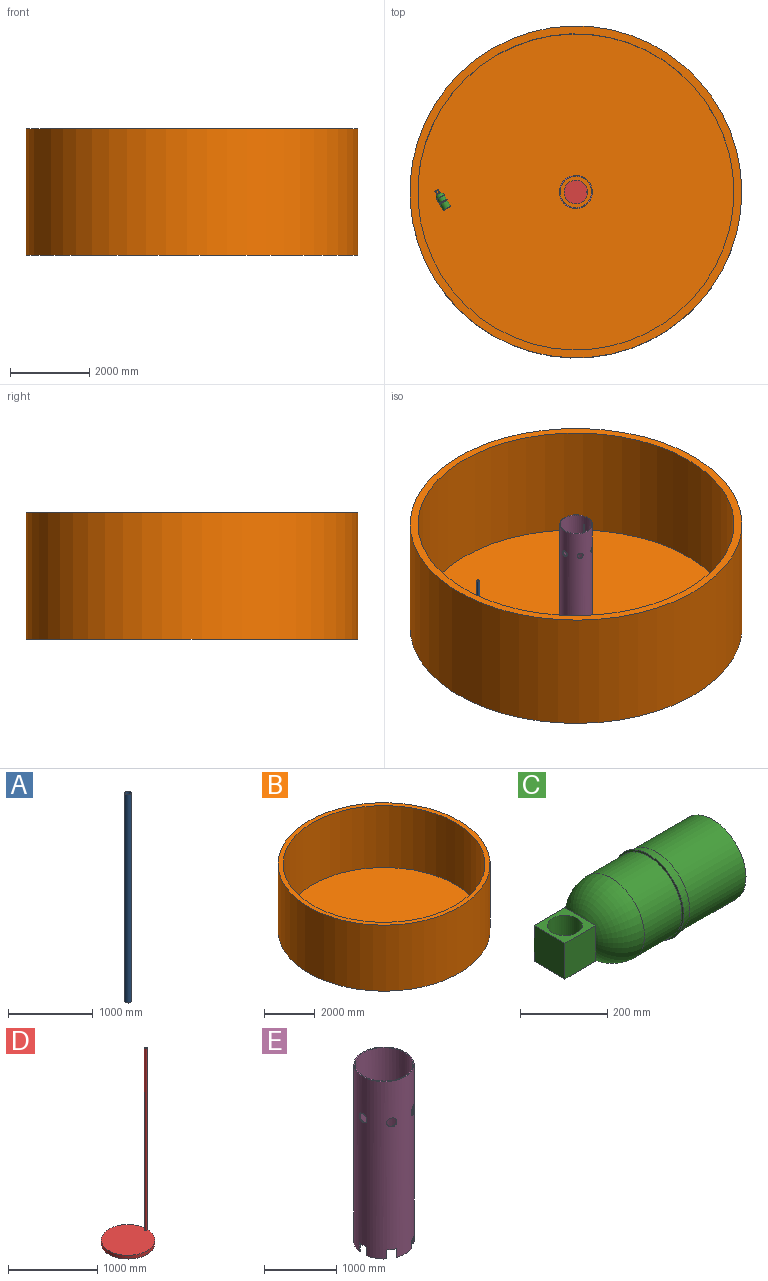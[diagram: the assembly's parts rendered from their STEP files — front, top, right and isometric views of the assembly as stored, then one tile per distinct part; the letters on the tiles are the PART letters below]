
ASSEMBLY  parts=5 mates=4
PART A: 4 faces, bbox 80x80x3000 mm
  f0: cylinder r=39mm len=3000mm, axis (0,0,-1), area 735132.7mm2, adj f2,f3
  f1: cylinder r=40mm len=3000mm, axis (0,0,-1), area 753982.2mm2, adj f2,f3
  f2: plane 80x80mm, normal (0,0,1), area 248.2mm2, adj f0,f1
  f3: plane 80x80mm, normal (0,0,-1), area 248.2mm2, adj f0,f1
PART B: 5 faces, bbox 8400x8400x3200 mm
  f0: cylinder r=4200mm len=8400mm, axis (0,0,1), area 84446010.5mm2, adj f1,f3
  f1: plane 8400x8400mm, normal (0,0,-1), area 55417694.4mm2, adj f0
  f2: cylinder r=4000mm len=8000mm, axis (0,0,-1), area 75398223.7mm2, adj f3,f4
  f3: plane 8400x8400mm, normal (0,0,1), area 5152212mm2, adj f0,f2
  f4: plane 8000x8000mm, normal (0,0,1), area 50265482.5mm2, adj f2
PART C: 13 faces, bbox 528x227x227 mm
  f0: cylinder r=108mm len=216mm, axis (1,0,0), area 82196.7mm2, adj f1,f5
  f1: torus R=8mm, axis (1,0,0), area 70123.6mm2, adj f0,f6
  f2: plane 216x216mm, normal (1,0,0), area 36643.5mm2, adj f3
  f3: cylinder r=108mm len=216mm, axis (1,0,0), area 123631.8mm2, adj f2,f4
  f4: cone r=113.5mm half-angle=12.4deg, axis (-1,0,0), area 17812.6mm2, adj f3,f5
  f5: plane 227x227mm, normal (-1,0,0), area 3827.2mm2, adj f0,f4
  f6: plane 100x100mm, normal (1,0,0), area 9195.8mm2, adj f1,f7,f9,f10,f11
  f7: plane 100x100mm, normal (0,1,0), area 10000mm2, adj f6,f8,f10,f11
  f8: plane 100x100mm, normal (-1,0,0), area 10000mm2, adj f7,f9,f10,f11
  f9: plane 100x100mm, normal (0,-1,0), area 10000mm2, adj f6,f8,f10,f11
  f10: plane 100x100mm, normal (0,0,1), area 4973.5mm2, adj f6,f7,f8,f9,f12
  f11: plane 100x100mm, normal (0,0,-1), area 4973.5mm2, adj f6,f7,f8,f9,f12
  f12: cylinder r=40mm len=100mm, axis (0,0,1), area 25132.7mm2, adj f10,f11
PART D: 7 faces, bbox 600x600x2550 mm
  f0: cylinder r=300mm len=600mm, axis (0,0,-1), area 94247.8mm2, adj f1,f2
  f1: plane 600x600mm, normal (0,0,1), area 281939.1mm2, adj f0,f4
  f2: plane 600x600mm, normal (0,0,-1), area 282743.3mm2, adj f0
  f3: cylinder r=14mm len=2500mm, axis (0,0,-1), area 219911.5mm2, adj f5,f6
  f4: cylinder r=16mm len=2500mm, axis (0,0,-1), area 251327.4mm2, adj f1,f5
  f5: plane 32x32mm, normal (0,0,1), area 188.5mm2, adj f3,f4
  f6: plane 28x28mm, normal (0,0,1), area 615.8mm2, adj f3
PART E: 33 faces, bbox 830x830x3000 mm
  f0: plane 129.95x83.55mm, normal (0,0,-1), area 2133.7mm2, adj f5,f6,f27,f31
  f1: plane 144.13x21.08mm, normal (0,0,-1), area 2133.7mm2, adj f5,f6,f24,f28
  f2: plane 129.95x83.55mm, normal (0,0,-1), area 2133.7mm2, adj f5,f6,f21,f25
  f3: plane 129.95x83.55mm, normal (0,0,-1), area 2133.7mm2, adj f5,f6,f18,f22
  f4: plane 144.13x21.08mm, normal (0,0,-1), area 2133.7mm2, adj f5,f6,f15,f19
  f5: cylinder r=415mm len=3000mm, axis (0,0,-1), area 7585657.5mm2, adj f0,f1,f2,f3,f4,f7,f8,f9
  f6: cylinder r=400mm len=3000mm, axis (0,0,-1), area 7307745.1mm2, adj f0,f1,f2,f3,f4,f7,f8,f9
  f7: plane 830x830mm, normal (0,0,1), area 38406mm2, adj f5,f6
  f8: plane 129.95x83.55mm, normal (0,0,-1), area 2133.7mm2, adj f5,f6,f16,f30
  f9: cylinder r=75mm len=150mm, axis (1,0,0), area 7130.8mm2, adj f5,f6
  f10: cylinder r=75mm len=150mm, axis (0.5,-0.87,0), area 7129.7mm2, adj f5,f6
  f11: cylinder r=75mm len=150mm, axis (-0.5,-0.87,0), area 7129.7mm2, adj f5,f6
  f12: cylinder r=75mm len=150mm, axis (-1,0,0), area 7129.7mm2, adj f5,f6
  f13: cylinder r=75mm len=150mm, axis (-0.5,0.87,0), area 7129.7mm2, adj f5,f6
  f14: cylinder r=75mm len=150mm, axis (0.5,0.87,0), area 7129.7mm2, adj f5,f6
  f15: plane 150x14.77mm, normal (0.17,-0.98,0), area 2250mm2, adj f4,f5,f6,f17
  f16: plane 150x11.49mm, normal (-0.77,0.64,0), area 2250mm2, adj f5,f6,f8,f17
  f17: plane 248.45x151.58mm, normal (0,0,-1), area 4267.3mm2, adj f5,f6,f15,f16
  f18: plane 150x11.49mm, normal (-0.77,-0.64,0), area 2250mm2, adj f3,f5,f6,f20
  f19: plane 150x14.77mm, normal (0.17,0.98,0), area 2250mm2, adj f4,f5,f6,f20
  f20: plane 248.45x151.58mm, normal (0,0,-1), area 4267.3mm2, adj f5,f6,f18,f19
  f21: plane 150x14.1mm, normal (-0.94,0.34,0), area 2250mm2, adj f2,f5,f6,f23
  f22: plane 150x14.1mm, normal (0.94,0.34,0), area 2250mm2, adj f3,f5,f6,f23
  f23: plane 283.88x39.12mm, normal (0,0,-1), area 4267.3mm2, adj f5,f6,f21,f22
  f24: plane 150x14.77mm, normal (-0.17,0.98,0), area 2250mm2, adj f1,f5,f6,f26
  f25: plane 150x11.49mm, normal (0.77,-0.64,0), area 2250mm2, adj f2,f5,f6,f26
  f26: plane 248.45x151.58mm, normal (0,0,-1), area 4267.3mm2, adj f5,f6,f24,f25
  f27: plane 150x11.49mm, normal (0.77,0.64,0), area 2250mm2, adj f0,f5,f6,f29
  f28: plane 150x14.77mm, normal (-0.17,-0.98,0), area 2250mm2, adj f1,f5,f6,f29
  f29: plane 248.45x151.58mm, normal (0,0,-1), area 4267.3mm2, adj f5,f6,f27,f28
  f30: plane 150x14.1mm, normal (0.94,-0.34,0), area 2250mm2, adj f5,f6,f8,f32
  f31: plane 150x14.1mm, normal (-0.94,-0.34,0), area 2250mm2, adj f0,f5,f6,f32
  f32: plane 283.88x39.12mm, normal (0,0,-1), area 4267.3mm2, adj f5,f6,f30,f31
PLACE A t=(-3500,0,0)mm
PLACE B at identity fixed
PLACE C rot(axis=(0.87,-0.5,0),180deg) t=(-3475,-43.3,1650.71)mm
PLACE D t=(0,0,300)mm
PLACE E t=(0,0,150)mm
MATE fastened B.f2 <-> E.f6  axis (0,0,1) through (0,0,0)mm
MATE cylindrical C.f12 <-> A.f0  axis (0,0,-1) through (-3500,0,1600.71)mm
MATE fastened D.f0 <-> B.f2  axis (0,0,-1) through (0,0,300)mm
MATE fastened B.f2 <-> A.f3  axis (0,0,1) through (0,0,0)mm
